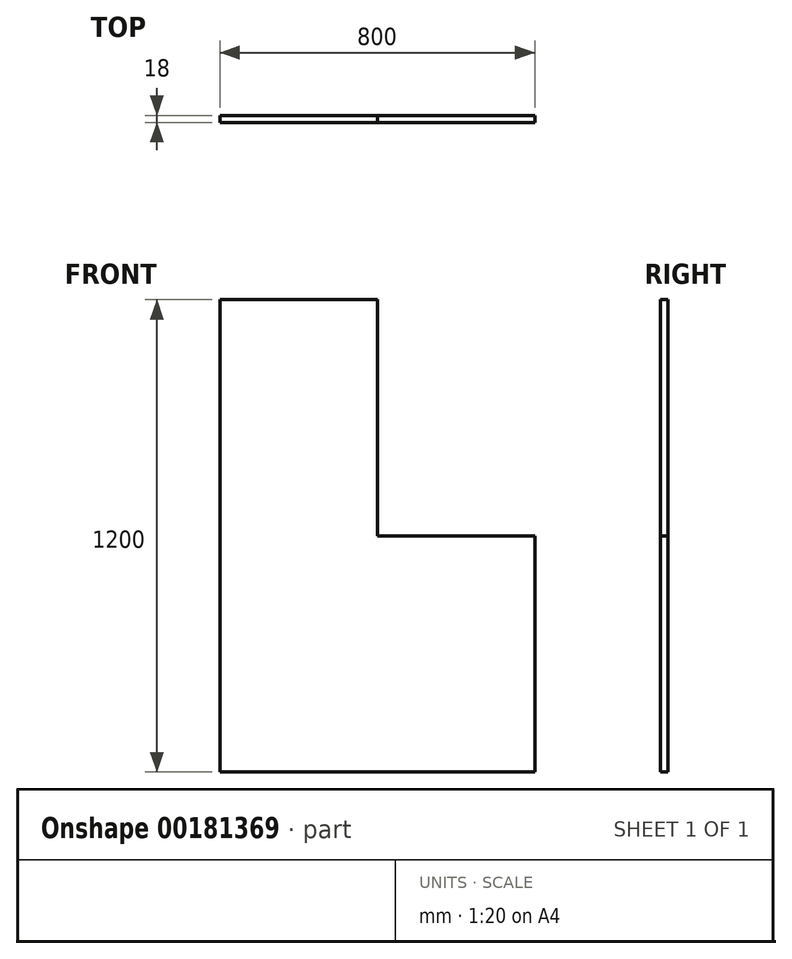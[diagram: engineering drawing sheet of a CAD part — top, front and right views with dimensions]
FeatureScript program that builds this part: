
annotation { "Feature Type Name" : "Feature", "Feature Type Description" : "" }
export const myFeature = defineFeature(function(context is Context, id is Id, definition is map)
    precondition{}
    {
        {
            var Q0;
            Q0=qCreatedBy(makeId("Front.planeOp"),FACE);
            var sketch = newSketch(context, id + "F0", { "sketchPlane" : qUnion([Q0])});
            skLineSegment(sketch, "E0", {"start": v(-400, -600) * mm, "end": v(400, -600) * mm});
            skLineSegment(sketch, "E1", {"start": v(400, -600) * mm, "end": v(400, 0) * mm});
            skLineSegment(sketch, "E2", {"start": v(400, 0) * mm, "end": v(0, 0) * mm});
            skLineSegment(sketch, "E3", {"start": v(0, 0) * mm, "end": v(0, 600) * mm});
            skLineSegment(sketch, "E4", {"start": v(0, 600) * mm, "end": v(-400, 600) * mm});
            skLineSegment(sketch, "E5", {"start": v(-400, 600) * mm, "end": v(-400, -600) * mm});
            skSolve(sketch);
        }
        {
            var Q0;
            Q0 = qSketchRegion(id + "F0", true);
            extrude(context, id + "F1", {"entities" : qUnion([Q0]), "depth" : 18 * mm});
        }
    });
